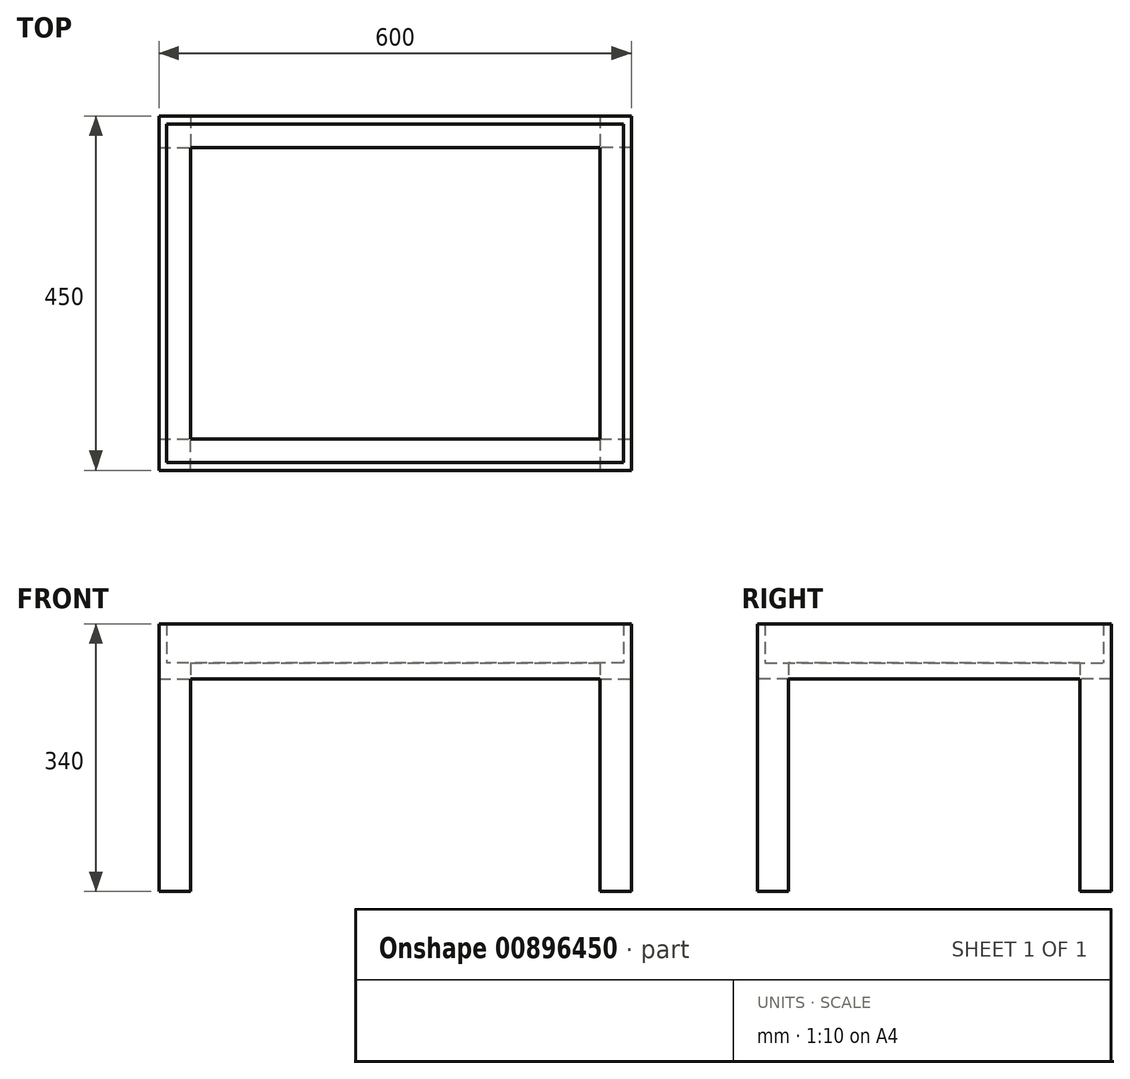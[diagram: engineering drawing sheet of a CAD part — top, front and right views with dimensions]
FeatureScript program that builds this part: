
annotation { "Feature Type Name" : "Feature", "Feature Type Description" : "" }
export const myFeature = defineFeature(function(context is Context, id is Id, definition is map)
    precondition{}
    {
        {
            var Q0;
            Q0=qCreatedBy(makeId("Top.planeOp"),FACE);
            var sketch = newSketch(context, id + "F0", { "sketchPlane" : qUnion([Q0])});
            skLineSegment(sketch, "E0.bottom", {"start": v(-300, 225) * mm, "end": v(300, 225) * mm});
            skLineSegment(sketch, "E0.top", {"start": v(-300, -225) * mm, "end": v(300, -225) * mm});
            skLineSegment(sketch, "E0.left", {"start": v(-300, 225) * mm, "end": v(-300, -225) * mm});
            skLineSegment(sketch, "E0.right", {"start": v(300, 225) * mm, "end": v(300, -225) * mm});
            skLineSegment(sketch, "E1.bottom", {"start": v(-260, 185) * mm, "end": v(260, 185) * mm});
            skLineSegment(sketch, "E1.top", {"start": v(-260, -185) * mm, "end": v(260, -185) * mm});
            skLineSegment(sketch, "E1.left", {"start": v(-260, 185) * mm, "end": v(-260, -185) * mm});
            skLineSegment(sketch, "E1.right", {"start": v(260, 185) * mm, "end": v(260, -185) * mm});
            skSolve(sketch);
        }
        {
            var Q0;
            Q0=makeQuery(id+"F0.imprint","IMPRINT",FACE,{"disambiguationData":[TD([[makeQuery(id+"F0.imprint","IMPRINT",EDGE,{"derivedFrom":sQuery(id+"F0.wireOp",EDGE,"E0.bottom")}),-1.0]])]});
            extrude(context, id + "F1", {"entities" : qUnion([Q0]), "flatOperationType" : FlatOperationType.REMOVE, "depth" : 20 * mm, "offsetDistance" : 25 * mm, "domain" : OperationDomain.MODEL});
        }
        {
            var Q0;
            Q0=makeQuery(id+"F1.opExtrude","CAP_FACE",FACE,{"disambiguationData":[OSD([sQuery(id+"F0.wireOp",EDGE,"E0.bottom"),sQuery(id+"F0.wireOp",EDGE,"E0.top"),sQuery(id+"F0.wireOp",EDGE,"E0.left"),sQuery(id+"F0.wireOp",EDGE,"E0.right"),sQuery(id+"F0.wireOp",EDGE,"E1.bottom"),sQuery(id+"F0.wireOp",EDGE,"E1.top"),sQuery(id+"F0.wireOp",EDGE,"E1.left"),sQuery(id+"F0.wireOp",EDGE,"E1.right")])],"isStart":false});
            var sketch = newSketch(context, id + "F2", { "sketchPlane" : qUnion([Q0])});
            skLineSegment(sketch, "E2.bottom", {"start": v(-300, 225) * mm, "end": v(300, 225) * mm});
            skLineSegment(sketch, "E2.top", {"start": v(-300, -225) * mm, "end": v(300, -225) * mm});
            skLineSegment(sketch, "E2.left", {"start": v(-300, 225) * mm, "end": v(-300, -225) * mm});
            skLineSegment(sketch, "E2.right", {"start": v(300, 225) * mm, "end": v(300, -225) * mm});
            skLineSegment(sketch, "E3.bottom", {"start": v(290, -215) * mm, "end": v(-290, -215) * mm});
            skLineSegment(sketch, "E3.top", {"start": v(290, 215) * mm, "end": v(-290, 215) * mm});
            skLineSegment(sketch, "E3.left", {"start": v(290, -215) * mm, "end": v(290, 215) * mm});
            skLineSegment(sketch, "E3.right", {"start": v(-290, -215) * mm, "end": v(-290, 215) * mm});
            skSolve(sketch);
        }
        {
            var Q0;
            Q0=makeQuery(id+"F2.imprint","IMPRINT",FACE,{"disambiguationData":[TD([[makeQuery(id+"F2.imprint","IMPRINT",EDGE,{"derivedFrom":sQuery(id+"F2.wireOp",EDGE,"E2.bottom")}),-1.0]])]});
            extrude(context, id + "F3", {"entities" : qUnion([Q0]), "operationType" : NewBodyOperationType.ADD, "depth" : 50 * mm, "offsetDistance" : 25 * mm});
        }
        {
            var Q0;
            Q0=makeQuery(id+"F1.opExtrude","CAP_FACE",FACE,{"disambiguationData":[OSD([sQuery(id+"F0.wireOp",EDGE,"E0.bottom"),sQuery(id+"F0.wireOp",EDGE,"E0.top"),sQuery(id+"F0.wireOp",EDGE,"E0.left"),sQuery(id+"F0.wireOp",EDGE,"E0.right"),sQuery(id+"F0.wireOp",EDGE,"E1.bottom"),sQuery(id+"F0.wireOp",EDGE,"E1.top"),sQuery(id+"F0.wireOp",EDGE,"E1.left"),sQuery(id+"F0.wireOp",EDGE,"E1.right")])],"isStart":true});
            var sketch = newSketch(context, id + "F4", { "sketchPlane" : qUnion([Q0])});
            skLineSegment(sketch, "E4.bottom", {"start": v(-300, 225) * mm, "end": v(-260, 225) * mm});
            skLineSegment(sketch, "E4.top", {"start": v(-300, 185) * mm, "end": v(-260, 185) * mm});
            skLineSegment(sketch, "E4.left", {"start": v(-300, 225) * mm, "end": v(-300, 185) * mm});
            skLineSegment(sketch, "E4.right", {"start": v(-260, 225) * mm, "end": v(-260, 185) * mm});
            skLineSegment(sketch, "E5.bottom", {"start": v(-300, -225) * mm, "end": v(-260, -225) * mm});
            skLineSegment(sketch, "E5.top", {"start": v(-300, -185) * mm, "end": v(-260, -185) * mm});
            skLineSegment(sketch, "E5.left", {"start": v(-300, -225) * mm, "end": v(-300, -185) * mm});
            skLineSegment(sketch, "E5.right", {"start": v(-260, -225) * mm, "end": v(-260, -185) * mm});
            skLineSegment(sketch, "E6.bottom", {"start": v(300, -225) * mm, "end": v(260, -225) * mm});
            skLineSegment(sketch, "E6.top", {"start": v(300, -185) * mm, "end": v(260, -185) * mm});
            skLineSegment(sketch, "E6.left", {"start": v(300, -225) * mm, "end": v(300, -185) * mm});
            skLineSegment(sketch, "E6.right", {"start": v(260, -225) * mm, "end": v(260, -185) * mm});
            skLineSegment(sketch, "E7.bottom", {"start": v(260, 185) * mm, "end": v(300, 185) * mm});
            skLineSegment(sketch, "E7.top", {"start": v(260, 225) * mm, "end": v(300, 225) * mm});
            skLineSegment(sketch, "E7.left", {"start": v(260, 185) * mm, "end": v(260, 225) * mm});
            skLineSegment(sketch, "E7.right", {"start": v(300, 185) * mm, "end": v(300, 225) * mm});
            skSolve(sketch);
        }
        {
            var Q0;
            Q0=makeQuery(id+"F4.imprint","IMPRINT",FACE,{"disambiguationData":[TD([[makeQuery(id+"F4.imprint","IMPRINT",EDGE,{"derivedFrom":sQuery(id+"F4.wireOp",EDGE,"E4.bottom")}),-1.0]])]});
            var Q1;
            Q1=makeQuery(id+"F4.imprint","IMPRINT",FACE,{"disambiguationData":[TD([[makeQuery(id+"F4.imprint","IMPRINT",EDGE,{"derivedFrom":sQuery(id+"F4.wireOp",EDGE,"E7.bottom")}),1.0]])]});
            var Q2;
            Q2=makeQuery(id+"F4.imprint","IMPRINT",FACE,{"disambiguationData":[TD([[makeQuery(id+"F4.imprint","IMPRINT",EDGE,{"derivedFrom":sQuery(id+"F4.wireOp",EDGE,"E6.bottom")}),1.0]])]});
            var Q3;
            Q3=makeQuery(id+"F4.imprint","IMPRINT",FACE,{"disambiguationData":[TD([[makeQuery(id+"F4.imprint","IMPRINT",EDGE,{"derivedFrom":sQuery(id+"F4.wireOp",EDGE,"E5.bottom")}),1.0]])]});
            extrude(context, id + "F5", {"entities" : qUnion([Q0, Q1, Q2, Q3]), "operationType" : NewBodyOperationType.ADD, "flatOperationType" : FlatOperationType.REMOVE, "depth" : 270 * mm, "offsetDistance" : 25 * mm, "domain" : OperationDomain.MODEL});
        }
    });
